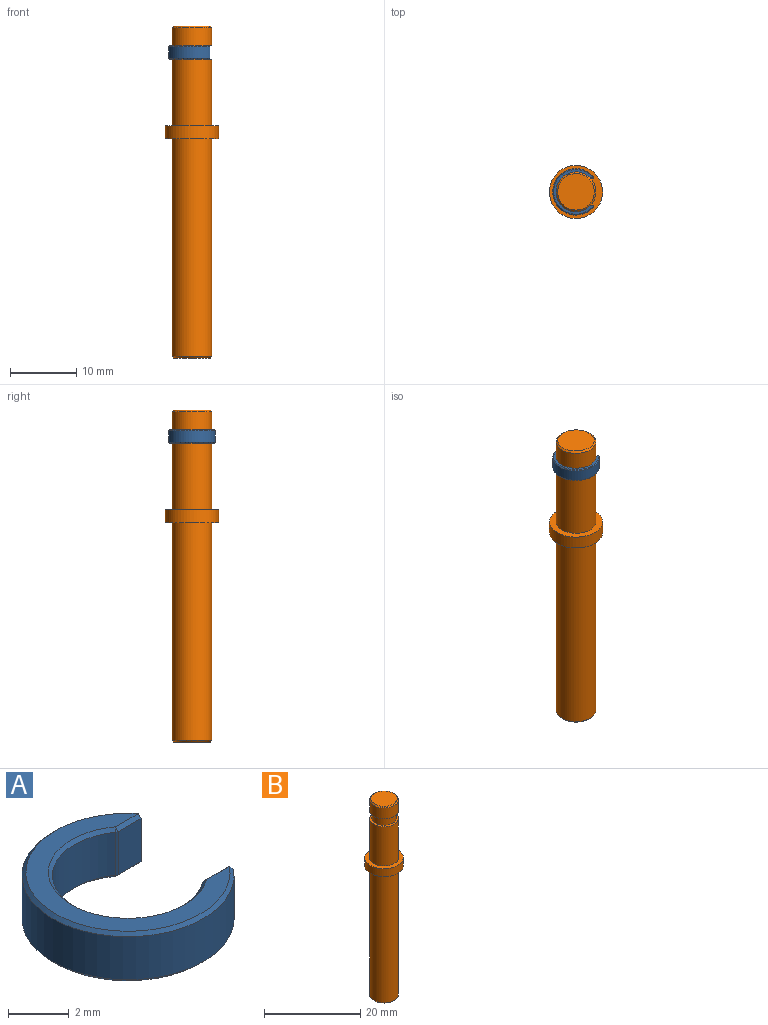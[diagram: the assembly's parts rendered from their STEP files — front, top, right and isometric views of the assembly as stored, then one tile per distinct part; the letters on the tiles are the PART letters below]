
ASSEMBLY  parts=2 mates=1
PART A: 26 faces, bbox 6.2x7x2 mm
  f0: plane 1.74x1.07mm, normal (0,-1,0), area 1.9mm2, adj f11,f20,f21,f25
  f1: cylinder r=3.5mm len=7mm, axis (0,0,-1), area 29.9mm2, adj f9,f10,f19,f20
  f2: plane 1.74x1.07mm, normal (0,1,0), area 1.9mm2, adj f6,f9,f13,f14
  f3: cylinder r=2.5mm len=5mm, axis (0,0,-1), area 19.1mm2, adj f12,f13,f21,f22
  f4: plane 6.74x5.98mm, normal (0,0,1), area 10.4mm2, adj f14,f19,f22,f25
  f5: plane 6.74x5.98mm, normal (0,0,-1), area 10.4mm2, adj f6,f10,f11,f12
  f6: plane 1.07x0.13mm, normal (0,0.71,-0.71), area 0.2mm2, adj f2,f5,f7,f8
  f7: plane 0.21x0.13mm, normal (0.83,0.39,-0.39), area 0mm2, adj f6,f9,f10
  f8: plane 0.13x0.13mm, normal (-0.22,0.69,-0.69), area 0mm2, adj f6,f12,f13
  f9: plane 1.74x0.21mm, normal (0.9,0.43,0), area 0.4mm2, adj f1,f2,f7,f15
  f10: cone r=3.5mm half-angle=45deg, axis (0,0,1), area 3.1mm2, adj f1,f5,f7,f16
  f11: plane 1.07x0.13mm, normal (0,-0.71,-0.71), area 0.2mm2, adj f0,f5,f16,f17
  f12: cone r=2.63mm half-angle=45deg, axis (0,0,-1), area 2.1mm2, adj f3,f5,f8,f17
  f13: plane 1.74x0.08mm, normal (-0.31,0.95,0), area 0.1mm2, adj f2,f3,f8,f18
  f14: plane 1.07x0.13mm, normal (0,0.71,0.71), area 0.2mm2, adj f2,f4,f15,f18
  f15: plane 0.21x0.13mm, normal (0.83,0.39,0.39), area 0mm2, adj f9,f14,f19
  f16: plane 0.21x0.13mm, normal (0.83,-0.39,-0.39), area 0mm2, adj f10,f11,f20
  f17: plane 0.13x0.13mm, normal (-0.22,-0.69,-0.69), area 0mm2, adj f11,f12,f21
  f18: plane 0.13x0.13mm, normal (-0.22,0.69,0.69), area 0mm2, adj f13,f14,f22
  f19: cone r=3.37mm half-angle=45deg, axis (0,0,-1), area 3.1mm2, adj f1,f4,f15,f23
  f20: plane 1.74x0.21mm, normal (0.9,-0.43,0), area 0.4mm2, adj f0,f1,f16,f23
  f21: plane 1.74x0.08mm, normal (-0.31,-0.95,0), area 0.1mm2, adj f0,f3,f17,f24
  f22: cone r=2.5mm half-angle=45deg, axis (0,0,1), area 2.1mm2, adj f3,f4,f18,f24
  f23: plane 0.21x0.13mm, normal (0.83,-0.39,0.39), area 0mm2, adj f19,f20,f25
  f24: plane 0.13x0.13mm, normal (-0.22,-0.69,0.69), area 0mm2, adj f21,f22,f25
  f25: plane 1.07x0.13mm, normal (0,-0.71,0.71), area 0.2mm2, adj f0,f4,f23,f24
PART B: 13 faces, bbox 8x8x50 mm
  f0: cylinder r=3mm len=6mm, axis (0,0,-1), area 51.8mm2, adj f3,f6
  f1: plane 5.5x5.5mm, normal (0,0,1), area 23.8mm2, adj f6
  f2: cylinder r=2.5mm len=5mm, axis (0,0,-1), area 31.4mm2, adj f3,f4
  f3: plane 6x6mm, normal (0,0,-1), area 8.6mm2, adj f0,f2
  f4: plane 6x6mm, normal (0,0,1), area 8.6mm2, adj f2,f5
  f5: cylinder r=3mm len=10mm, axis (0,0,-1), area 188.5mm2, adj f4,f8
  f6: cone r=2.75mm half-angle=45deg, axis (0,0,-1), area 6.4mm2, adj f0,f1
  f7: cylinder r=4mm len=8mm, axis (0,0,-1), area 50.3mm2, adj f8,f9
  f8: plane 8x8mm, normal (0,0,1), area 22mm2, adj f5,f7
  f9: plane 8x8mm, normal (0,0,-1), area 22mm2, adj f7,f12
  f10: plane 5.5x5.5mm, normal (0,0,-1), area 23.8mm2, adj f11
  f11: cone r=3mm half-angle=45deg, axis (0,0,1), area 6.4mm2, adj f10,f12
  f12: cylinder r=3mm len=32.75mm, axis (0,0,-1), area 617.3mm2, adj f9,f11
PLACE A t=(0.16,3.01,21.03)mm
PLACE B t=(0.16,-41.99,0.03)mm fixed
MATE fastened A.f3 <-> B.f0  axis (0,0,-1) through (0.16,3.01,21.03)mm
